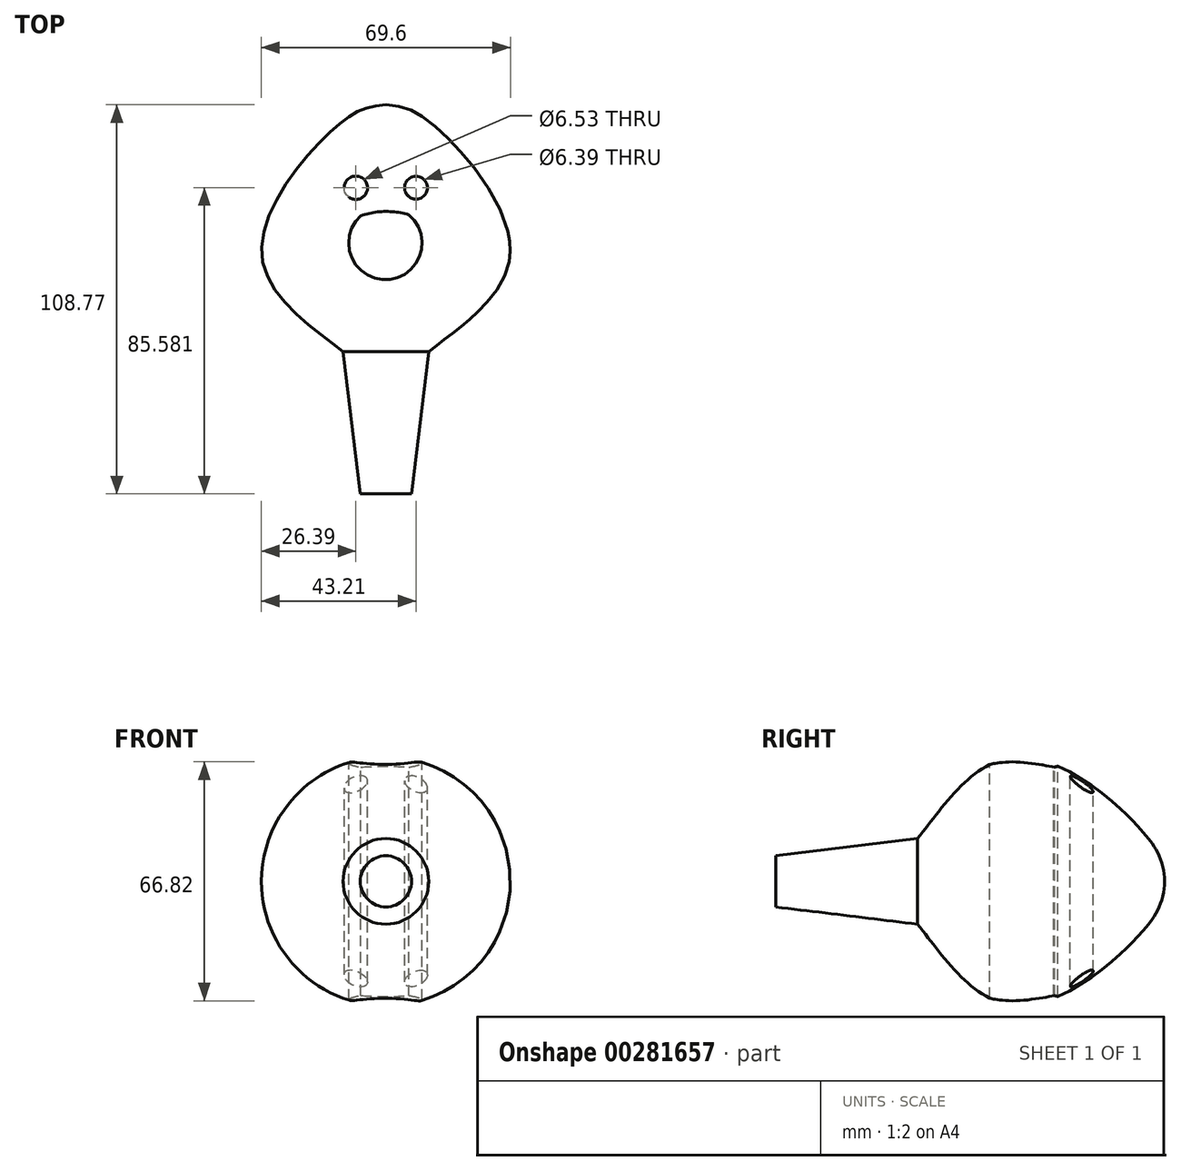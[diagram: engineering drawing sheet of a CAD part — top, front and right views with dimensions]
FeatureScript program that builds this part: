
annotation { "Feature Type Name" : "Feature", "Feature Type Description" : "" }
export const myFeature = defineFeature(function(context is Context, id is Id, definition is map)
    precondition{}
    {
        {
            var Q0;
            Q0=qCreatedBy(makeId("Top.planeOp"),FACE);
            var sketch = newSketch(context, id + "F0", { "sketchPlane" : qUnion([Q0])});
            skLineSegment(sketch, "E0", {"start": v(-11.98, 0) * mm, "end": v(-7.16, -39.7) * mm});
            skLineSegment(sketch, "E1", {"start": v(-7.16, -39.7) * mm, "end": v(0, -39.7) * mm});
            skLineSegment(sketch, "E2", {"start": v(0, -39.7) * mm, "end": v(0, 0) * mm});
            skLineSegment(sketch, "E3", {"start": v(0, -39.7) * mm, "end": v(0, 69.06) * mm});
            skFitSpline(sketch, "E4", {"points": [v(-11.98, 0) * mm, v(-34.66, 26.25) * mm, v(-14.78, 62.18) * mm, v(0, 69.06) * mm], "startDerivative": vector(-61.44, 49.44) * mm, "endDerivative": vector(70.41, 3.57) * mm});
            skSolve(sketch);
        }
        {
            var Q0;
            Q0=makeQuery(id+"F0.imprint","IMPRINT",FACE,{"disambiguationData":[TD([[makeQuery(id+"F0.imprint","IMPRINT",EDGE,{"derivedFrom":sQuery(id+"F0.wireOp",EDGE,"E0")}),1.0]])]});
            var Q1;
            Q1=sQuery(id+"F0.wireOp",EDGE,"E3");
            revolve(context, id + "F1", {"entities" : qUnion([Q0]), "axis" : qUnion([Q1]), "revolveType" : RevolveType.FULL});
        }
        {
            var Q0;
            Q0=qCreatedBy(makeId("Top.planeOp"),FACE);
            var sketch = newSketch(context, id + "F2", { "sketchPlane" : qUnion([Q0])});
            skCircle(sketch, "E5", {"center": v(-8.41, 45.87) * mm, "radius": 3.26 * mm});
            skCircle(sketch, "E6", {"center": v(8.41, 45.87) * mm, "radius": 3.2 * mm});
            skArc(sketch, "E7", {"start": v(-7, 38.06) * mm, "mid": v(0.05, 20.16) * mm, "end": v(6.44, 38.31) * mm});
            skArc(sketch, "E8", {"start": v(6.44, 38.31) * mm, "mid": v(-0.3, 39.22) * mm, "end": v(-7, 38.06) * mm});
            skSolve(sketch);
        }
        {
            var Q0;
            Q0 = qSketchRegion(id + "F2", true);
            extrude(context, id + "F3", {"entities" : qUnion([Q0]), "operationType" : NewBodyOperationType.REMOVE, "endBound" : BoundingType.THROUGH_ALL, "oppositeDirection" : true, "depth" : 25 * mm});
        }
        {
            var Q0;
            Q0 = qSketchRegion(id + "F2", true);
            extrude(context, id + "F4", {"entities" : qUnion([Q0]), "operationType" : NewBodyOperationType.REMOVE, "endBound" : BoundingType.THROUGH_ALL, "depth" : 25 * mm});
        }
    });
